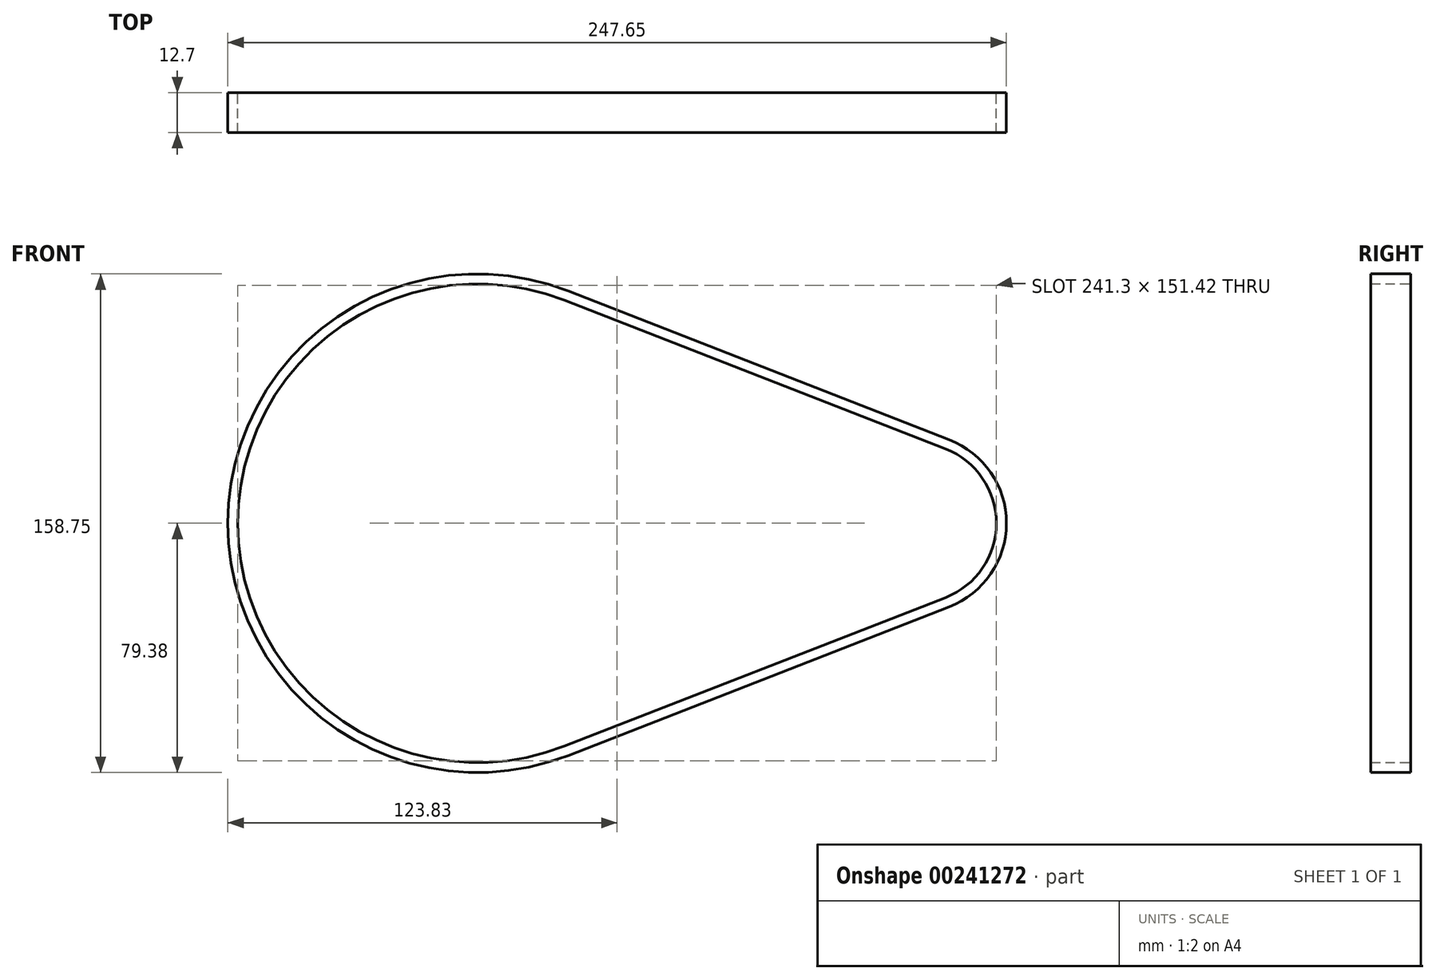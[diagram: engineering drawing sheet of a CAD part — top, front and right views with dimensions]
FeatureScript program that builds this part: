
annotation { "Feature Type Name" : "Feature", "Feature Type Description" : "" }
export const myFeature = defineFeature(function(context is Context, id is Id, definition is map)
    precondition{}
    {
        {
            var Q0;
            Q0=qCreatedBy(makeId("Front.planeOp"),FACE);
            var sketch = newSketch(context, id + "F0", { "sketchPlane" : qUnion([Q0])});
            skCircle(sketch, "E0", {"center": v(0, 0) * mm, "radius": 76.2 * mm});
            skCircle(sketch, "E1", {"center": v(139.7, 0) * mm, "radius": 25.4 * mm});
            skCircle(sketch, "E2", {"center": v(0, 0) * mm, "radius": 79.38 * mm});
            skCircle(sketch, "E3", {"center": v(139.7, 0) * mm, "radius": 28.58 * mm});
            skLineSegment(sketch, "E4", {"start": v(27.7, 70.98) * mm, "end": v(148.94, 23.66) * mm});
            skLineSegment(sketch, "E5", {"start": v(27.7, -70.98) * mm, "end": v(148.94, -23.66) * mm});
            skLineSegment(sketch, "E6", {"start": v(28.86, 73.94) * mm, "end": v(150.1, 26.62) * mm});
            skLineSegment(sketch, "E7", {"start": v(150.1, -26.62) * mm, "end": v(28.86, -73.94) * mm});
            skSolve(sketch);
        }
        {
            var Q0;
            Q0=qSketchRegion(id+"F0",true);
            extrude(context, id + "F1", {"entities" : qUnion([Q0]), "depth" : 12.7 * mm});
        }
    });
